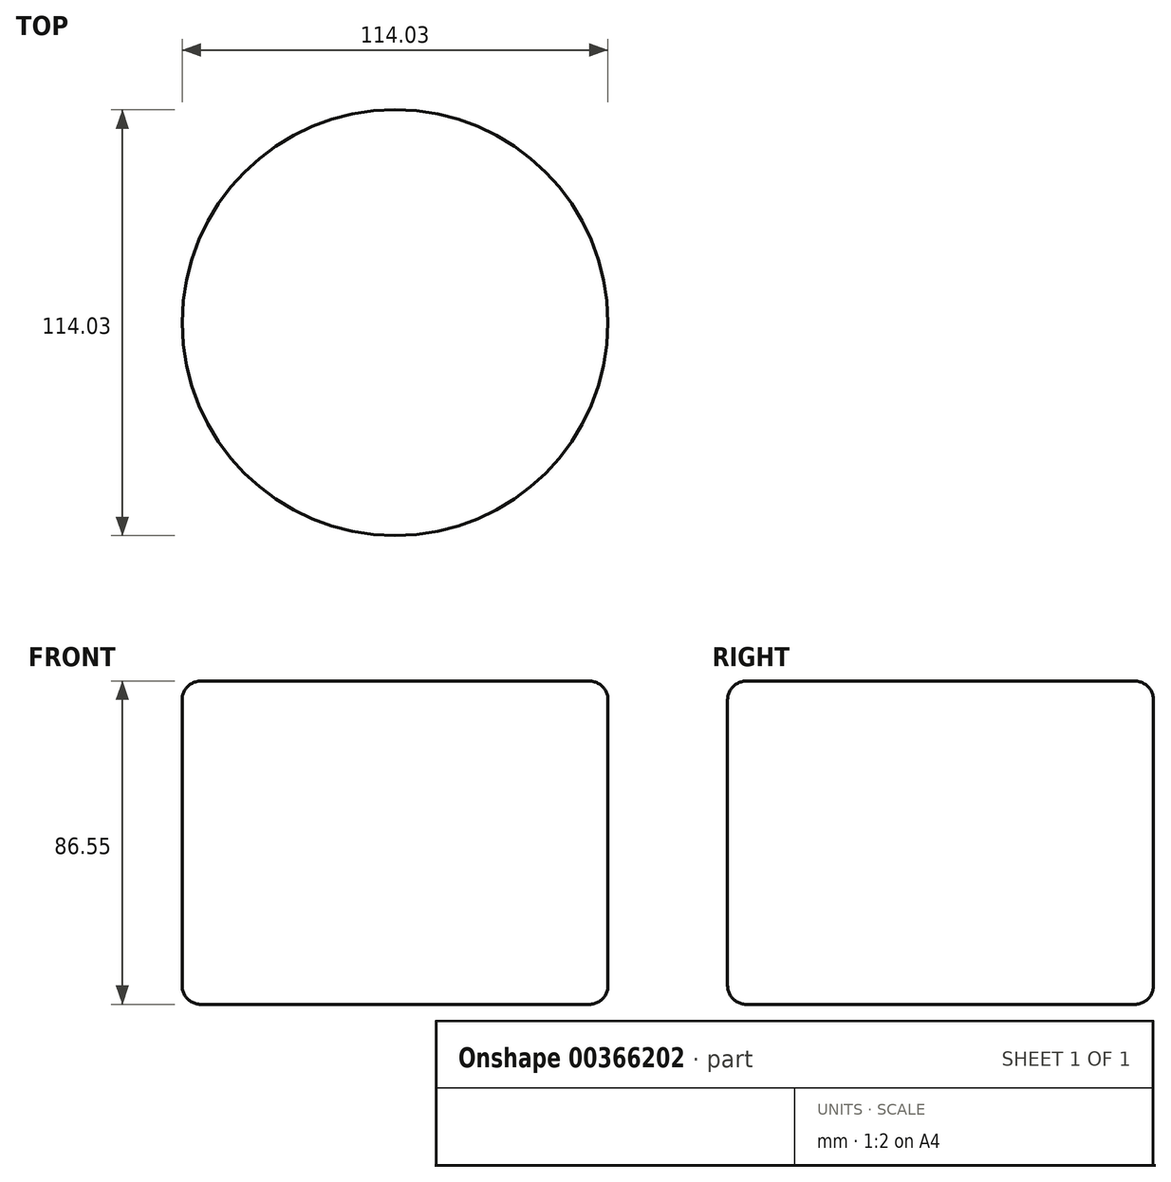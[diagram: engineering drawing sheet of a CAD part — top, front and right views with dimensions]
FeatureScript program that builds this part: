
annotation { "Feature Type Name" : "Feature", "Feature Type Description" : "" }
export const myFeature = defineFeature(function(context is Context, id is Id, definition is map)
    precondition{}
    {
        {
            var Q0;
            Q0=qCreatedBy(makeId("Top.planeOp"),FACE);
            var sketch = newSketch(context, id + "F0", { "sketchPlane" : qUnion([Q0])});
            skCircle(sketch, "E0", {"center": v(-34.83, 26.53) * mm, "radius": 57.02 * mm});
            skSolve(sketch);
        }
        {
            var Q0;
            Q0=makeQuery(id+"F0.imprint","IMPRINT",FACE,{"disambiguationData":[TD([[makeQuery(id+"F0.imprint","IMPRINT",EDGE,{"derivedFrom":sQuery(id+"F0.wireOp",EDGE,"E0")}),1.0]])]});
            var Q1;
            Q1 = qSketchRegion(id + "F0", true);
            extrude(context, id + "F1", {"entities" : qUnion([Q0, Q1]), "depth" : 86.55 * mm});
        }
        {
            var Q0;
            Q0=makeQuery(id+"F1.opExtrude","CAP_EDGE",EDGE,{"disambiguationData":[OSD([sQuery(id+"F0.wireOp",EDGE,"E0")])],"isStart":false});
            var Q1;
            Q1=makeQuery(id+"F1.opExtrude","CAP_EDGE",EDGE,{"disambiguationData":[OSD([sQuery(id+"F0.wireOp",EDGE,"E0")])],"isStart":true});
            fillet(context, id + "F2", {"entities" : qUnion([Q0, Q1]), "radius" : 5 * mm, "tangentPropagation" : true, "allowEdgeOverflow" : false});
        }
    });
